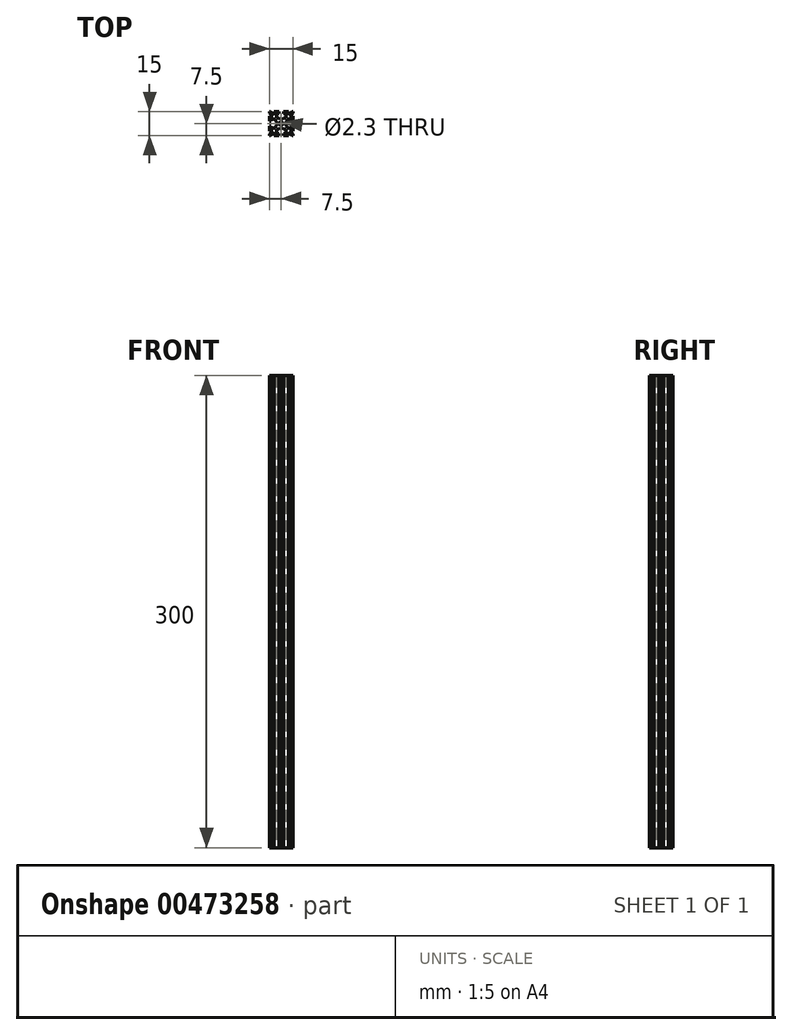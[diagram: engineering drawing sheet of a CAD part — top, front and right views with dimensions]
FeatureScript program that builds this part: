
annotation { "Feature Type Name" : "Feature", "Feature Type Description" : "" }
export const myFeature = defineFeature(function(context is Context, id is Id, definition is map)
    precondition{}
    {
        {
            var Q0;
            Q0=qCreatedBy(makeId("Top.planeOp"),FACE);
            var sketch = newSketch(context, id + "F0", { "sketchPlane" : qUnion([Q0]), "disableImprinting" : false});
            skLineSegment(sketch, "E0", {"start": v(0, 0) * mm, "end": v(-7.5, 0) * mm, "construction": true});
            skLineSegment(sketch, "E1", {"start": v(-7.5, 1.5) * mm, "end": v(-7.5, 4.63) * mm});
            skLineSegment(sketch, "E2", {"start": v(0, 7.5) * mm, "end": v(0, 0) * mm, "construction": true});
            skArc(sketch, "E3", {"start": v(0, 1.15) * mm, "mid": v(-0.81, 0.81) * mm, "end": v(-1.15, 0) * mm});
            skLineSegment(sketch, "E4", {"start": v(0, 0) * mm, "end": v(-7.5, 7.5) * mm, "construction": true});
            skLineSegment(sketch, "E5.top", {"start": v(-7.5, 1.5) * mm, "end": v(-6.5, 1.5) * mm});
            skLineSegment(sketch, "E5.left", {"start": v(-7.5, 7.5) * mm, "end": v(-7.5, 6.8) * mm});
            skLineSegment(sketch, "E6", {"start": v(-6.5, 1.5) * mm, "end": v(-6.5, 3) * mm});
            skLineSegment(sketch, "E7", {"start": v(-6.5, 3) * mm, "end": v(-3.65, 3) * mm});
            skLineSegment(sketch, "E8", {"start": v(-3.65, 3) * mm, "end": v(-3.65, 1.5) * mm});
            skLineSegment(sketch, "E9", {"start": v(-3.65, 1.5) * mm, "end": v(-2.71, 0.81) * mm});
            skLineSegment(sketch, "E10", {"start": v(-2.71, 0.81) * mm, "end": v(-2.71, 0) * mm});
            skLineSegment(sketch, "E11", {"start": v(-7.5, 6.8) * mm, "end": v(-5.34, 4.63) * mm});
            skLineSegment(sketch, "E12", {"start": v(-5.34, 4.63) * mm, "end": v(-7.5, 4.63) * mm});
            skLineSegment(sketch, "E13.trimOffspring", {"start": v(-7.5, 4.63) * mm, "end": v(-7.5, 1.5) * mm});
            skLineSegment(sketch, "E14.trimOffspring", {"start": v(-7.5, 6.8) * mm, "end": v(-7.5, 7.5) * mm});
            skLineSegment(sketch, "E15.MirrorCS", {"start": v(-1.5, 7.5) * mm, "end": v(-4.63, 7.5) * mm});
            skLineSegment(sketch, "E16.MirrorCS", {"start": v(-7.5, 7.5) * mm, "end": v(-6.8, 7.5) * mm});
            skLineSegment(sketch, "E17.MirrorCS", {"start": v(-6.8, 7.5) * mm, "end": v(-7.5, 7.5) * mm});
            skLineSegment(sketch, "E18.MirrorCS", {"start": v(-4.63, 7.5) * mm, "end": v(-1.5, 7.5) * mm});
            skLineSegment(sketch, "E19.MirrorCS", {"start": v(-6.8, 7.5) * mm, "end": v(-4.63, 5.34) * mm});
            skLineSegment(sketch, "E20.MirrorCS", {"start": v(-3, 3.65) * mm, "end": v(-1.5, 3.65) * mm});
            skLineSegment(sketch, "E21.MirrorCS", {"start": v(-1.5, 3.65) * mm, "end": v(-0.81, 2.71) * mm});
            skLineSegment(sketch, "E22.MirrorCS", {"start": v(-3, 6.5) * mm, "end": v(-3, 3.65) * mm});
            skLineSegment(sketch, "E23.MirrorCS", {"start": v(-1.5, 7.5) * mm, "end": v(-1.5, 6.5) * mm});
            skLineSegment(sketch, "E24.MirrorCS", {"start": v(-1.5, 6.5) * mm, "end": v(-3, 6.5) * mm});
            skLineSegment(sketch, "E25.MirrorCS", {"start": v(-4.63, 5.34) * mm, "end": v(-4.63, 7.5) * mm});
            skLineSegment(sketch, "E26.MirrorCS", {"start": v(-0.81, 2.71) * mm, "end": v(0, 2.71) * mm});
            skLineSegment(sketch, "E27.MirrorCS", {"start": v(7.5, 4.63) * mm, "end": v(7.5, 1.5) * mm});
            skLineSegment(sketch, "E28.MirrorCS", {"start": v(7.5, 6.8) * mm, "end": v(7.5, 7.5) * mm});
            skLineSegment(sketch, "E29.MirrorCS", {"start": v(7.5, 7.5) * mm, "end": v(6.8, 7.5) * mm});
            skLineSegment(sketch, "E30.MirrorCS", {"start": v(4.63, 7.5) * mm, "end": v(1.5, 7.5) * mm});
            skLineSegment(sketch, "E31.MirrorCS", {"start": v(1.5, 7.5) * mm, "end": v(4.63, 7.5) * mm});
            skLineSegment(sketch, "E32.MirrorCS", {"start": v(6.8, 7.5) * mm, "end": v(7.5, 7.5) * mm});
            skLineSegment(sketch, "E33.MirrorCS", {"start": v(6.8, 7.5) * mm, "end": v(4.63, 5.34) * mm});
            skLineSegment(sketch, "E34.MirrorCS", {"start": v(1.5, 3.65) * mm, "end": v(0.81, 2.71) * mm});
            skLineSegment(sketch, "E35.MirrorCS", {"start": v(3, 6.5) * mm, "end": v(3, 3.65) * mm});
            skLineSegment(sketch, "E36.MirrorCS", {"start": v(1.5, 6.5) * mm, "end": v(3, 6.5) * mm});
            skLineSegment(sketch, "E37.MirrorCS", {"start": v(0.81, 2.71) * mm, "end": v(0, 2.71) * mm});
            skLineSegment(sketch, "E38.MirrorCS", {"start": v(7.5, 6.8) * mm, "end": v(5.34, 4.63) * mm});
            skLineSegment(sketch, "E39.MirrorCS", {"start": v(2.71, 0.81) * mm, "end": v(2.71, 0) * mm});
            skLineSegment(sketch, "E40.MirrorCS", {"start": v(3.65, 1.5) * mm, "end": v(2.71, 0.81) * mm});
            skLineSegment(sketch, "E41.MirrorCS", {"start": v(3.65, 3) * mm, "end": v(3.65, 1.5) * mm});
            skLineSegment(sketch, "E42.MirrorCS", {"start": v(6.5, 3) * mm, "end": v(3.65, 3) * mm});
            skLineSegment(sketch, "E43.MirrorCS", {"start": v(6.5, 1.5) * mm, "end": v(6.5, 3) * mm});
            skLineSegment(sketch, "E44.MirrorCS", {"start": v(7.5, 7.5) * mm, "end": v(7.5, 6.8) * mm});
            skLineSegment(sketch, "E45.MirrorCS", {"start": v(7.5, 1.5) * mm, "end": v(6.5, 1.5) * mm});
            skLineSegment(sketch, "E46.MirrorCS", {"start": v(0, 0) * mm, "end": v(7.5, 7.5) * mm, "construction": true});
            skLineSegment(sketch, "E47.MirrorCS", {"start": v(7.5, 1.5) * mm, "end": v(7.5, 4.63) * mm});
            skArc(sketch, "E48.MirrorCS", {"start": v(0, 1.15) * mm, "mid": v(0.81, 0.81) * mm, "end": v(1.15, 0) * mm});
            skLineSegment(sketch, "E49.MirrorCS", {"start": v(0, 0) * mm, "end": v(7.5, 0) * mm, "construction": true});
            skLineSegment(sketch, "E50.MirrorCS", {"start": v(5.34, 4.63) * mm, "end": v(7.5, 4.63) * mm});
            skLineSegment(sketch, "E51.MirrorCS", {"start": v(4.63, 5.34) * mm, "end": v(4.63, 7.5) * mm});
            skLineSegment(sketch, "E52.MirrorCS", {"start": v(1.5, 7.5) * mm, "end": v(1.5, 6.5) * mm});
            skLineSegment(sketch, "E53.MirrorCS", {"start": v(3, 3.65) * mm, "end": v(1.5, 3.65) * mm});
            skLineSegment(sketch, "E54.MirrorCS", {"start": v(-4.63, -7.5) * mm, "end": v(-1.5, -7.5) * mm});
            skLineSegment(sketch, "E55.MirrorCS", {"start": v(1.5, -3.65) * mm, "end": v(0.81, -2.71) * mm});
            skLineSegment(sketch, "E56.MirrorCS", {"start": v(-7.5, -4.63) * mm, "end": v(-7.5, -1.5) * mm});
            skLineSegment(sketch, "E57.MirrorCS", {"start": v(-7.5, -6.8) * mm, "end": v(-7.5, -7.5) * mm});
            skLineSegment(sketch, "E58.MirrorCS", {"start": v(7.5, -7.5) * mm, "end": v(7.5, -6.8) * mm});
            skLineSegment(sketch, "E59.MirrorCS", {"start": v(-7.5, -7.5) * mm, "end": v(-6.8, -7.5) * mm});
            skLineSegment(sketch, "E60.MirrorCS", {"start": v(7.5, -7.5) * mm, "end": v(6.8, -7.5) * mm});
            skLineSegment(sketch, "E61.MirrorCS", {"start": v(1.5, -7.5) * mm, "end": v(4.63, -7.5) * mm});
            skLineSegment(sketch, "E62.MirrorCS", {"start": v(7.5, -1.5) * mm, "end": v(7.5, -4.63) * mm});
            skLineSegment(sketch, "E63.MirrorCS", {"start": v(3.65, -3) * mm, "end": v(3.65, -1.5) * mm});
            skLineSegment(sketch, "E64.MirrorCS", {"start": v(-4.63, -5.34) * mm, "end": v(-4.63, -7.5) * mm});
            skLineSegment(sketch, "E65.MirrorCS", {"start": v(5.34, -4.63) * mm, "end": v(7.5, -4.63) * mm});
            skLineSegment(sketch, "E66.MirrorCS", {"start": v(-5.34, -4.63) * mm, "end": v(-7.5, -4.63) * mm});
            skLineSegment(sketch, "E67.MirrorCS", {"start": v(-7.5, -1.5) * mm, "end": v(-7.5, -4.63) * mm});
            skLineSegment(sketch, "E68.MirrorCS", {"start": v(0, -7.5) * mm, "end": v(0, 0) * mm, "construction": true});
            skArc(sketch, "E69.MirrorCS", {"start": v(0, -1.15) * mm, "mid": v(-0.81, -0.81) * mm, "end": v(-1.15, 0) * mm});
            skLineSegment(sketch, "E70.MirrorCS", {"start": v(0, 0) * mm, "end": v(-7.5, -7.5) * mm, "construction": true});
            skLineSegment(sketch, "E71.MirrorCS", {"start": v(-7.5, -1.5) * mm, "end": v(-6.5, -1.5) * mm});
            skLineSegment(sketch, "E72.MirrorCS", {"start": v(-7.5, -7.5) * mm, "end": v(-7.5, -6.8) * mm});
            skLineSegment(sketch, "E73.MirrorCS", {"start": v(-6.5, -1.5) * mm, "end": v(-6.5, -3) * mm});
            skLineSegment(sketch, "E74.MirrorCS", {"start": v(-6.5, -3) * mm, "end": v(-3.65, -3) * mm});
            skLineSegment(sketch, "E75.MirrorCS", {"start": v(-3.65, -3) * mm, "end": v(-3.65, -1.5) * mm});
            skLineSegment(sketch, "E76.MirrorCS", {"start": v(-3.65, -1.5) * mm, "end": v(-2.71, -0.81) * mm});
            skLineSegment(sketch, "E77.MirrorCS", {"start": v(-2.71, -0.81) * mm, "end": v(-2.71, 0) * mm});
            skLineSegment(sketch, "E78.MirrorCS", {"start": v(-7.5, -6.8) * mm, "end": v(-5.34, -4.63) * mm});
            skLineSegment(sketch, "E79.MirrorCS", {"start": v(6.5, -3) * mm, "end": v(3.65, -3) * mm});
            skLineSegment(sketch, "E80.MirrorCS", {"start": v(-0.81, -2.71) * mm, "end": v(0, -2.71) * mm});
            skLineSegment(sketch, "E81.MirrorCS", {"start": v(7.5, -6.8) * mm, "end": v(5.34, -4.63) * mm});
            skLineSegment(sketch, "E82.MirrorCS", {"start": v(-3, -6.5) * mm, "end": v(-3, -3.65) * mm});
            skLineSegment(sketch, "E83.MirrorCS", {"start": v(-6.8, -7.5) * mm, "end": v(-4.63, -5.34) * mm});
            skLineSegment(sketch, "E84.MirrorCS", {"start": v(4.63, -5.34) * mm, "end": v(4.63, -7.5) * mm});
            skLineSegment(sketch, "E85.MirrorCS", {"start": v(7.5, -6.8) * mm, "end": v(7.5, -7.5) * mm});
            skLineSegment(sketch, "E86.MirrorCS", {"start": v(3, -6.5) * mm, "end": v(3, -3.65) * mm});
            skLineSegment(sketch, "E87.MirrorCS", {"start": v(-1.5, -7.5) * mm, "end": v(-4.63, -7.5) * mm});
            skLineSegment(sketch, "E88.MirrorCS", {"start": v(6.8, -7.5) * mm, "end": v(4.63, -5.34) * mm});
            skLineSegment(sketch, "E89.MirrorCS", {"start": v(6.8, -7.5) * mm, "end": v(7.5, -7.5) * mm});
            skLineSegment(sketch, "E90.MirrorCS", {"start": v(0, 0) * mm, "end": v(7.5, -7.5) * mm, "construction": true});
            skArc(sketch, "E91.MirrorCS", {"start": v(0, -1.15) * mm, "mid": v(0.81, -0.81) * mm, "end": v(1.15, 0) * mm});
            skLineSegment(sketch, "E92.MirrorCS", {"start": v(1.5, -6.5) * mm, "end": v(3, -6.5) * mm});
            skLineSegment(sketch, "E93.MirrorCS", {"start": v(7.5, -1.5) * mm, "end": v(6.5, -1.5) * mm});
            skLineSegment(sketch, "E94.MirrorCS", {"start": v(1.5, -7.5) * mm, "end": v(1.5, -6.5) * mm});
            skLineSegment(sketch, "E95.MirrorCS", {"start": v(-3, -3.65) * mm, "end": v(-1.5, -3.65) * mm});
            skLineSegment(sketch, "E96.MirrorCS", {"start": v(-1.5, -7.5) * mm, "end": v(-1.5, -6.5) * mm});
            skLineSegment(sketch, "E97.MirrorCS", {"start": v(2.71, -0.81) * mm, "end": v(2.71, 0) * mm});
            skLineSegment(sketch, "E98.MirrorCS", {"start": v(7.5, -4.63) * mm, "end": v(7.5, -1.5) * mm});
            skLineSegment(sketch, "E99.MirrorCS", {"start": v(6.5, -1.5) * mm, "end": v(6.5, -3) * mm});
            skLineSegment(sketch, "E100.MirrorCS", {"start": v(-6.8, -7.5) * mm, "end": v(-7.5, -7.5) * mm});
            skLineSegment(sketch, "E101.MirrorCS", {"start": v(3, -3.65) * mm, "end": v(1.5, -3.65) * mm});
            skLineSegment(sketch, "E102.MirrorCS", {"start": v(4.63, -7.5) * mm, "end": v(1.5, -7.5) * mm});
            skLineSegment(sketch, "E103.MirrorCS", {"start": v(-1.5, -6.5) * mm, "end": v(-3, -6.5) * mm});
            skLineSegment(sketch, "E104.MirrorCS", {"start": v(3.65, -1.5) * mm, "end": v(2.71, -0.81) * mm});
            skLineSegment(sketch, "E105.MirrorCS", {"start": v(0.81, -2.71) * mm, "end": v(0, -2.71) * mm});
            skLineSegment(sketch, "E106.MirrorCS", {"start": v(-1.5, -3.65) * mm, "end": v(-0.81, -2.71) * mm});
            skSolve(sketch);
        }
        {
            var Q0;
            Q0 = qSketchRegion(id + "F0", true);
            extrude(context, id + "F1", {"entities" : qUnion([Q0]), "depth" : 300 * mm});
        }
    });
